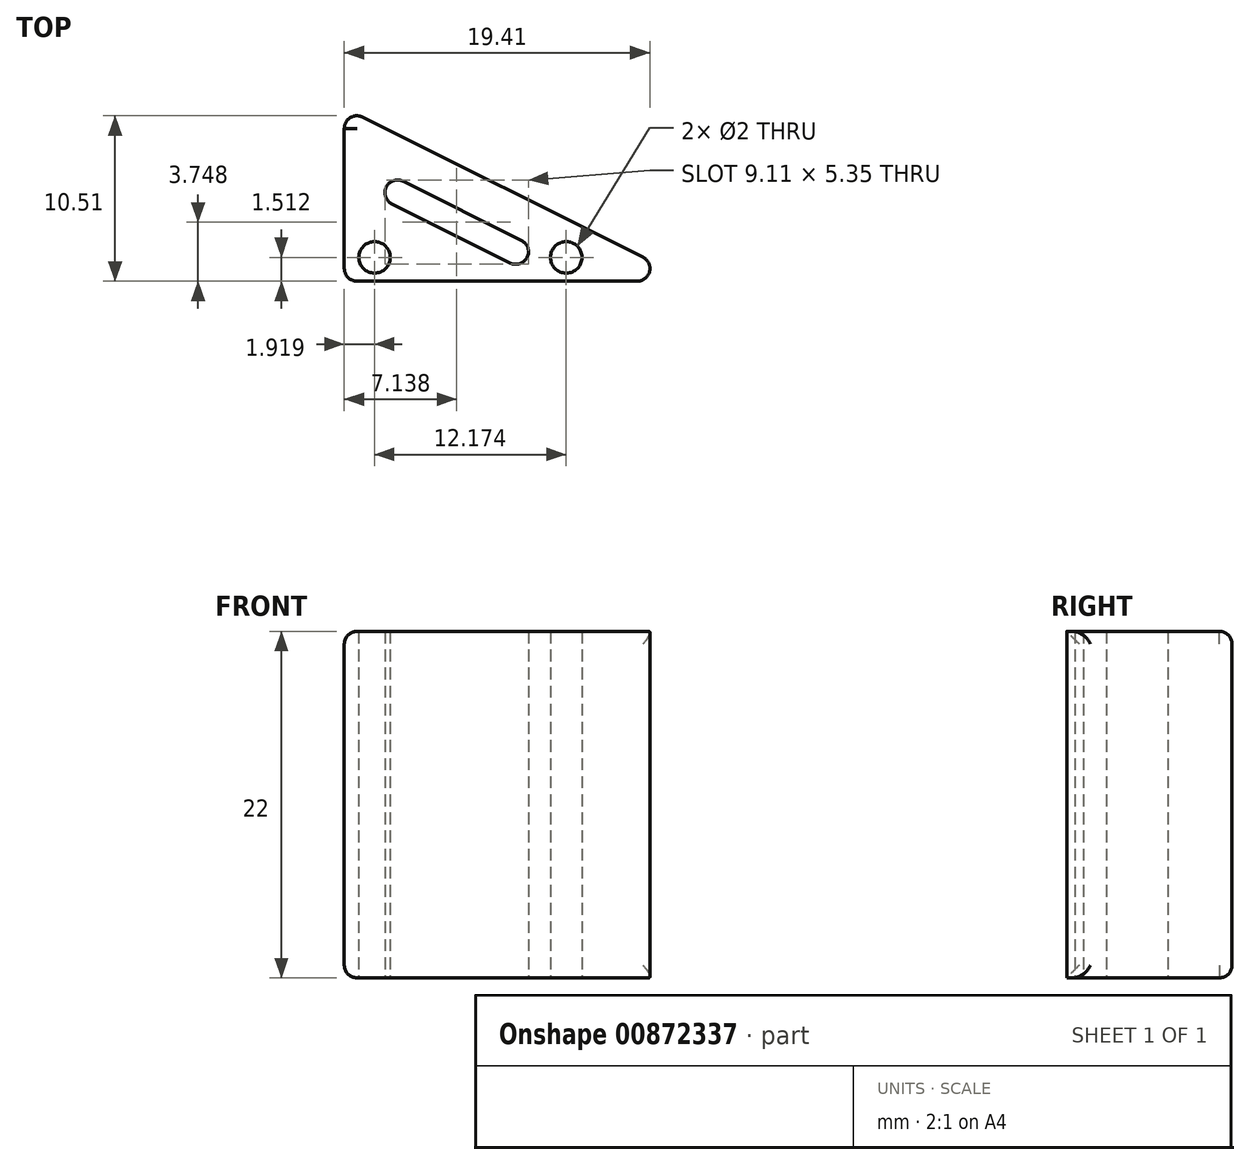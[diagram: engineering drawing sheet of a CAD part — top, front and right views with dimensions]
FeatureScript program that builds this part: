
annotation { "Feature Type Name" : "Feature", "Feature Type Description" : "" }
export const myFeature = defineFeature(function(context is Context, id is Id, definition is map)
    precondition{}
    {
        {
            var Q0;
            Q0=qCreatedBy(makeId("Top.planeOp"),FACE);
            var sketch = newSketch(context, id + "F0", { "sketchPlane" : qUnion([Q0])});
            skLineSegment(sketch, "E0.bottom", {"start": v(0, 0) * mm, "end": v(20, 0) * mm});
            skLineSegment(sketch, "E0.left", {"start": v(0, 0) * mm, "end": v(0, 10) * mm});
            skPoint(sketch, "E1.orphan", {"position": v(20, 10) * mm});
            skPoint(sketch, "E0.right.end.orphan", {"position": v(20, 5) * mm});
            skPoint(sketch, "E0.top.end.orphan", {"position": v(10, 10) * mm});
            skPoint(sketch, "E2.start.orphan", {"position": v(10, 5) * mm});
            skPoint(sketch, "E3.end.orphan", {"position": v(9.42, 3.85) * mm});
            skLineSegment(sketch, "E4", {"start": v(9.28, 3.57) * mm, "end": v(11.97, 2.23) * mm});
            skLineSegment(sketch, "E5", {"start": v(11.97, 2.23) * mm, "end": v(11.25, 0.8) * mm});
            skLineSegment(sketch, "E6", {"start": v(11.25, 0.8) * mm, "end": v(7.05, 2.9) * mm});
            skPoint(sketch, "E6.endSnap0", {"position": v(10.63, 2.9) * mm});
            skLineSegment(sketch, "E7", {"start": v(9.28, 3.57) * mm, "end": v(3.02, 6.7) * mm});
            skLineSegment(sketch, "E8", {"start": v(3.02, 6.7) * mm, "end": v(2.3, 5.27) * mm});
            skLineSegment(sketch, "E9", {"start": v(2.3, 5.27) * mm, "end": v(4.34, 4.25) * mm});
            skLineSegment(sketch, "E10", {"start": v(4.34, 4.25) * mm, "end": v(7.05, 2.9) * mm});
            skLineSegment(sketch, "E11", {"start": v(14.1, 1.51) * mm, "end": v(1.92, 1.51) * mm});
            skPoint(sketch, "E11.startSnap0", {"position": v(11.6, 1.51) * mm});
            skCircle(sketch, "E12", {"center": v(1.92, 1.51) * mm, "radius": 1 * mm});
            skCircle(sketch, "E13", {"center": v(14.1, 1.51) * mm, "radius": 1 * mm});
            skLineSegment(sketch, "E14", {"start": v(0, 10) * mm, "end": v(0, 11) * mm});
            skLineSegment(sketch, "E15", {"start": v(0, 11) * mm, "end": v(8.68, 6.66) * mm});
            skLineSegment(sketch, "E16", {"start": v(8.68, 6.66) * mm, "end": v(22, 0) * mm});
            skLineSegment(sketch, "E17", {"start": v(22, 0) * mm, "end": v(20, 0) * mm});
            skSolve(sketch);
        }
        {
            var Q0;
            Q0 = qSketchRegion(id + "F0", true);
            extrude(context, id + "F1", {"entities" : qUnion([Q0]), "depth" : 22 * mm, "offsetDistance" : 25 * mm});
        }
        {
            var Q0;
            Q0=makeQuery(id+"F1.opExtrude","SWEPT_EDGE",EDGE,{"disambiguationData":[OSD([sQuery(id+"F0.wireOp",EDGE,"E8"),sQuery(id+"F0.wireOp",EDGE,"E9")])]});
            var Q1;
            Q1=makeQuery(id+"F1.opExtrude","SWEPT_EDGE",EDGE,{"disambiguationData":[OSD([sQuery(id+"F0.wireOp",EDGE,"E7"),sQuery(id+"F0.wireOp",EDGE,"E8")])]});
            var Q2;
            Q2=makeQuery(id+"F1.opExtrude","SWEPT_EDGE",EDGE,{"disambiguationData":[OSD([sQuery(id+"F0.wireOp",EDGE,"E4"),sQuery(id+"F0.wireOp",EDGE,"E5")])]});
            var Q3;
            Q3=makeQuery(id+"F1.opExtrude","SWEPT_EDGE",EDGE,{"disambiguationData":[OSD([sQuery(id+"F0.wireOp",EDGE,"E5"),sQuery(id+"F0.wireOp",EDGE,"E6")])]});
            var Q4;
            Q4=makeQuery(id+"F1.opExtrude","CAP_EDGE",EDGE,{"disambiguationData":[OSD([sQuery(id+"F0.wireOp",EDGE,"E0.left")])],"isStart":false});
            var Q5;
            Q5=makeQuery(id+"F1.opExtrude","CAP_EDGE",EDGE,{"disambiguationData":[OSD([sQuery(id+"F0.wireOp",EDGE,"E0.left")])],"isStart":true});
            var Q6;
            Q6=makeQuery(id+"F1.opExtrude","SWEPT_EDGE",EDGE,{"disambiguationData":[OSD([sQuery(id+"F0.wireOp",EDGE,"E0.bottom"),sQuery(id+"F0.wireOp",EDGE,"92MxzUis-f4AS-sXPK-6Zv7-ptv3DloVmhnd")])]});
            var Q7;
            Q7=makeQuery(id+"F1.opExtrude","SWEPT_EDGE",EDGE,{"disambiguationData":[OSD([sQuery(id+"F0.wireOp",EDGE,"E0.left"),sQuery(id+"F0.wireOp",EDGE,"92MxzUis-f4AS-sXPK-6Zv7-ptv3DloVmhnd")])]});
            fillet(context, id + "F2", {"entities" : qUnion([Q0, Q1, Q2, Q3, Q4, Q5, Q6, Q7]), "radius" : .8 * mm, "tangentPropagation" : true, "allowEdgeOverflow" : false});
        }
        {
            var Q0;
            Q0=makeQuery(id+"F1.opExtrude","SWEPT_EDGE",EDGE,{"disambiguationData":[OSD([sQuery(id+"F0.wireOp",EDGE,"E14"),sQuery(id+"F0.wireOp",EDGE,"E15")])]});
            var Q1;
            Q1=makeQuery(id+"F1.opExtrude","SWEPT_EDGE",EDGE,{"disambiguationData":[OSD([sQuery(id+"F0.wireOp",EDGE,"E16"),sQuery(id+"F0.wireOp",EDGE,"E17")])]});
            fillet(context, id + "F3", {"entities" : qUnion([Q0, Q1]), "radius" : 0.8 * mm, "tangentPropagation" : true, "allowEdgeOverflow" : false});
        }
    });
